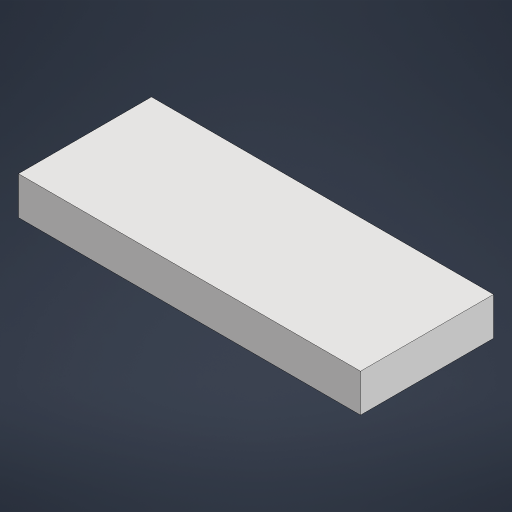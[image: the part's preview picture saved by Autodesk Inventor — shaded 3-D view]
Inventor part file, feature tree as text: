
AUTODESK INVENTOR PART (.ipt)
format: ipt  version: 2023.2 (Build 272271000, 271)  size: 149,504 bytes
history: native  units: in
note: dims shown in document units (in); Inventor stores cm internally (conversion verified against a paired STEP export)
features: extrude x1, sketch x1
ambient origin geometry x8: Origin, YZ Plane, XZ Plane, XY Plane, X Axis, Y Axis, Z Axis, Center Point
bodies: Solid1 (feature_tree)
feature tree (2):
  extrude  "Extrusion1"  Depth=7.0in
  sketch  "Sketch2"  dims[d3=2.0in d4=7.0in d5=18.0in d6=0.0in]
